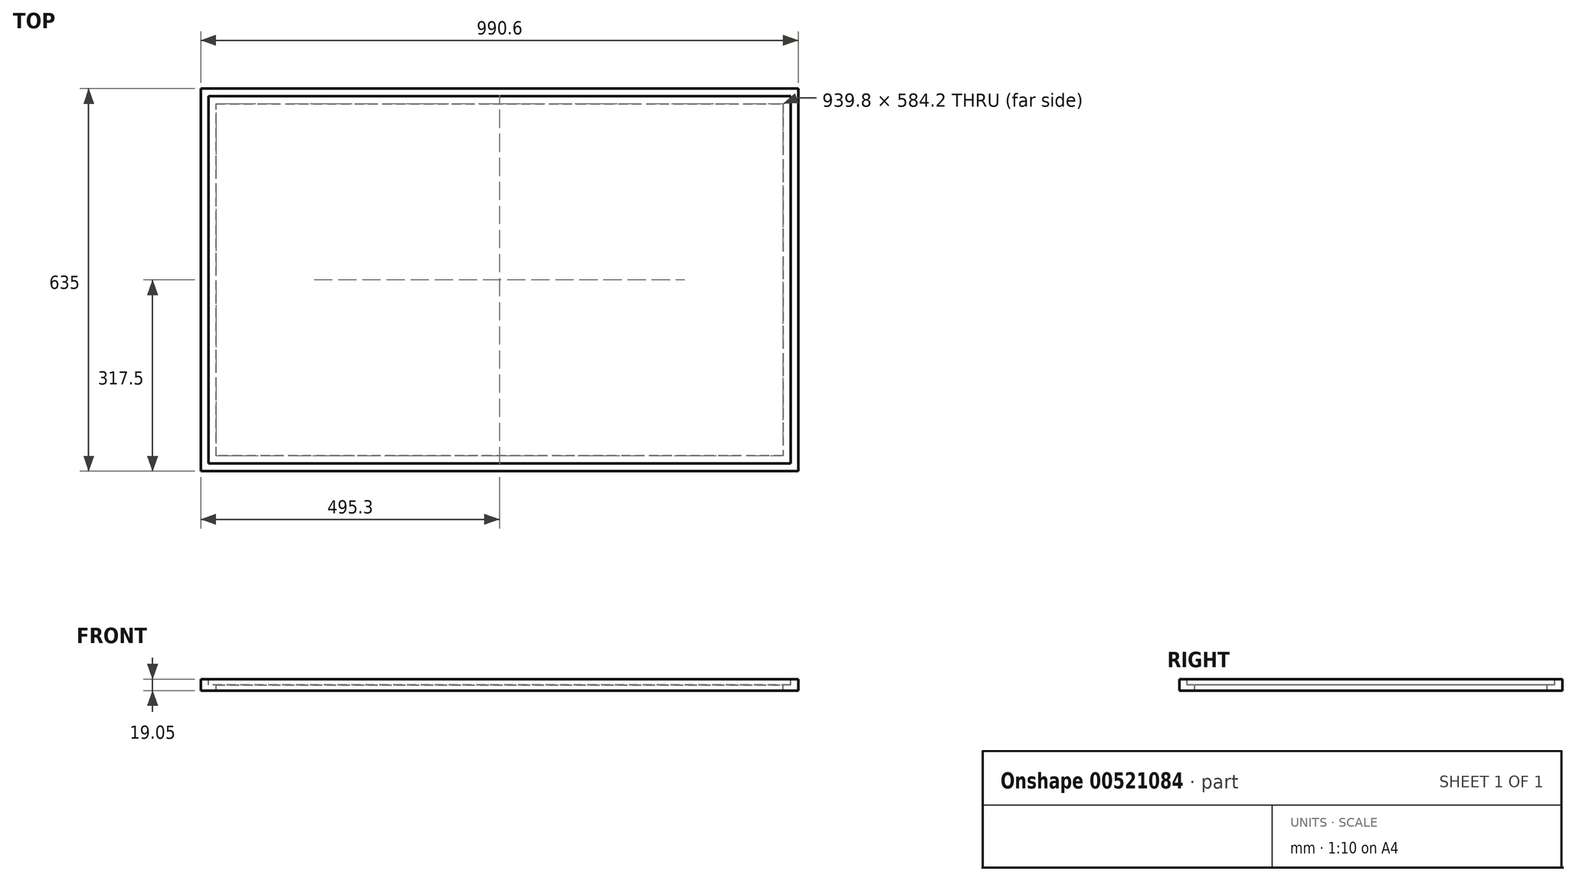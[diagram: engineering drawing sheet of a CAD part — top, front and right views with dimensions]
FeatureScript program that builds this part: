
annotation { "Feature Type Name" : "Feature", "Feature Type Description" : "" }
export const myFeature = defineFeature(function(context is Context, id is Id, definition is map)
    precondition{}
    {
        {
            var Q0;
            Q0=qCreatedBy(makeId("Top.planeOp"),FACE);
            var sketch = newSketch(context, id + "F0", { "sketchPlane" : qUnion([Q0])});
            skLineSegment(sketch, "E0", {"start": v(0, 367.77) * mm, "end": v(0, -381.09) * mm, "construction": true});
            skLineSegment(sketch, "E1", {"start": v(-624.05, 0) * mm, "end": v(634.04, 0) * mm, "construction": true});
            skLineSegment(sketch, "E2.bottom", {"start": v(-482.6, 304.8) * mm, "end": v(482.6, 304.8) * mm});
            skLineSegment(sketch, "E2.top", {"start": v(-482.6, -304.8) * mm, "end": v(482.6, -304.8) * mm});
            skLineSegment(sketch, "E2.left", {"start": v(-482.6, 304.8) * mm, "end": v(-482.6, -304.8) * mm});
            skLineSegment(sketch, "E2.right", {"start": v(482.6, 304.8) * mm, "end": v(482.6, -304.8) * mm});
            skSolve(sketch);
        }
        {
            var Q0;
            Q0 = qSketchRegion(id + "F0", true);
            extrude(context, id + "F1", {"entities" : qUnion([Q0]), "endBound" : BoundingType.SYMMETRIC, "depth" : 9.52 * mm, "offsetDistance" : 25.4 * mm});
        }
        {
            var Q0;
            Q0=qCreatedBy(makeId("Front.planeOp"),FACE);
            var sketch = newSketch(context, id + "F2", { "sketchPlane" : qUnion([Q0])});
            skLineSegment(sketch, "E3.0.0", {"start": v(-482.6, -4.76) * mm, "end": v(482.6, -4.76) * mm});
            skLineSegment(sketch, "E3.0.1", {"start": v(482.6, -4.76) * mm, "end": v(482.6, 4.76) * mm});
            skLineSegment(sketch, "E3.0.2", {"start": v(482.6, 4.76) * mm, "end": v(-482.6, 4.76) * mm});
            skLineSegment(sketch, "E3.0.3", {"start": v(-482.6, 4.76) * mm, "end": v(-482.6, -4.76) * mm});
            skLineSegment(sketch, "E4.bottom", {"start": v(482.6, 4.76) * mm, "end": v(495.3, 4.76) * mm});
            skLineSegment(sketch, "E4.top", {"start": v(482.6, -14.29) * mm, "end": v(495.3, -14.29) * mm});
            skLineSegment(sketch, "E4.left", {"start": v(482.6, 4.76) * mm, "end": v(482.6, -14.29) * mm});
            skLineSegment(sketch, "E4.right", {"start": v(495.3, 4.76) * mm, "end": v(495.3, -14.29) * mm});
            skLineSegment(sketch, "E5.bottom", {"start": v(482.6, -14.29) * mm, "end": v(469.9, -14.29) * mm});
            skLineSegment(sketch, "E5.top", {"start": v(482.6, -4.76) * mm, "end": v(469.9, -4.76) * mm});
            skLineSegment(sketch, "E5.left", {"start": v(482.6, -14.29) * mm, "end": v(482.6, -4.76) * mm});
            skLineSegment(sketch, "E5.right", {"start": v(469.9, -14.29) * mm, "end": v(469.9, -4.76) * mm});
            skSolve(sketch);
        }
        {
            var Q0;
            Q0=makeQuery(id+"F2.imprint","IMPRINT",FACE,{"disambiguationData":[TD([[makeQuery(id+"F2.imprint","IMPRINT",EDGE,{"derivedFrom":sQuery(id+"F2.wireOp",EDGE,"E4.bottom")}),-1.0]])]});
            var Q1;
            Q1=makeQuery(id+"F2.imprint","IMPRINT",FACE,{"disambiguationData":[TD([[makeQuery(id+"F2.imprint","IMPRINT",EDGE,{"derivedFrom":sQuery(id+"F2.wireOp",EDGE,"E5.bottom")}),-1.0]])]});
            var Q2;
            Q2=makeQuery(id+"F1.opExtrude","CAP_EDGE",EDGE,{"disambiguationData":[OSD([sQuery(id+"F0.wireOp",EDGE,"E2.right")])],"isStart":false});
            var Q3;
            Q3=makeQuery(id+"F1.opExtrude","CAP_EDGE",EDGE,{"disambiguationData":[OSD([sQuery(id+"F0.wireOp",EDGE,"E2.bottom")])],"isStart":false});
            var Q4;
            Q4=makeQuery(id+"F1.opExtrude","CAP_EDGE",EDGE,{"disambiguationData":[OSD([sQuery(id+"F0.wireOp",EDGE,"E2.top")])],"isStart":false});
            var Q5;
            Q5=makeQuery(id+"F1.opExtrude","CAP_EDGE",EDGE,{"disambiguationData":[OSD([sQuery(id+"F0.wireOp",EDGE,"E2.left")])],"isStart":false});
            sweep(context, id + "F3", {"profiles" : qUnion([Q0, Q1]), "path" : qUnion([Q2, Q3, Q4, Q5])});
        }
    });
